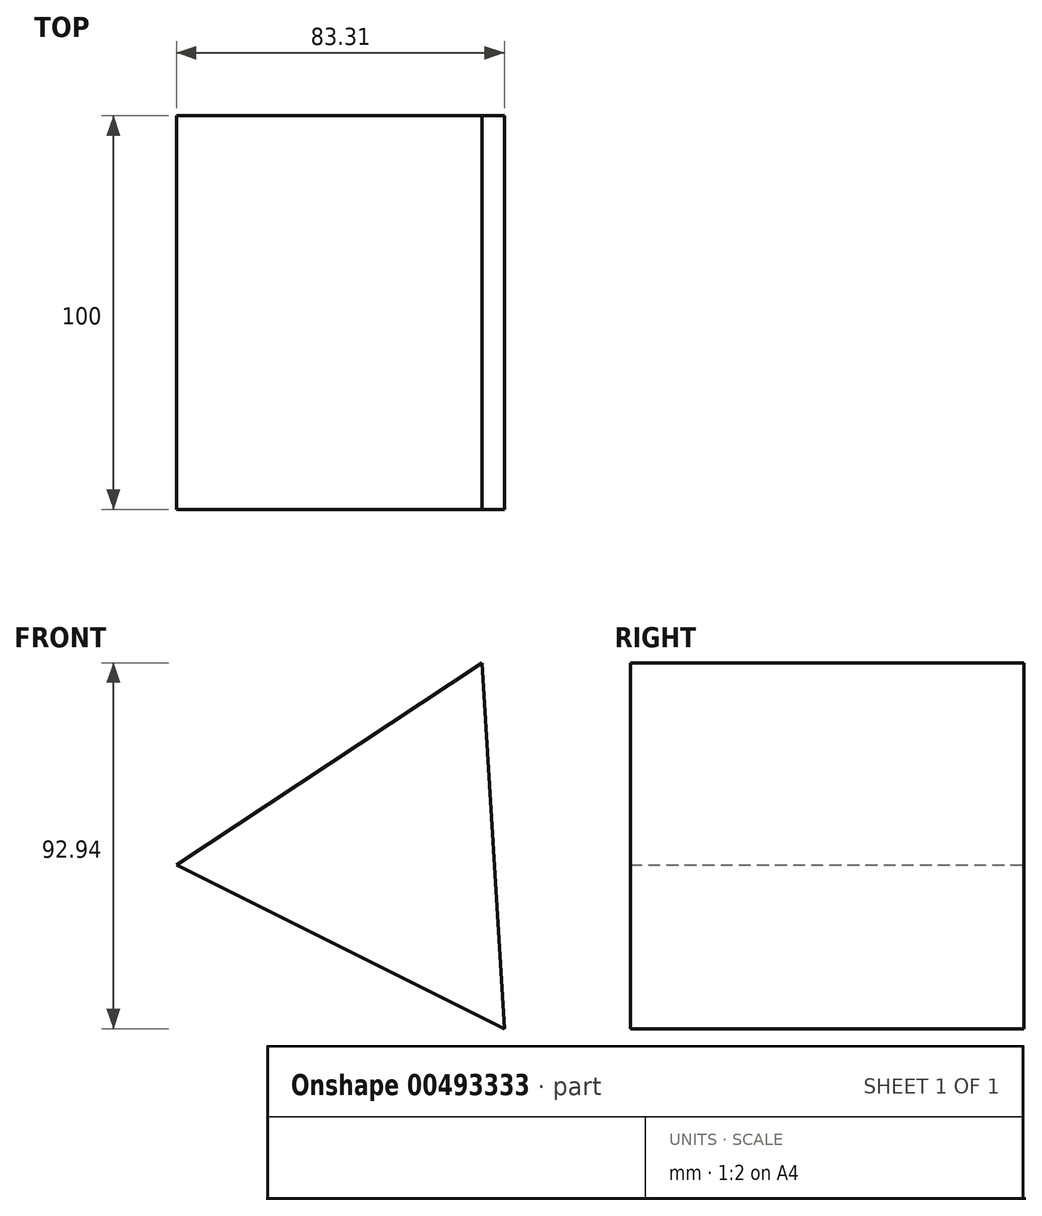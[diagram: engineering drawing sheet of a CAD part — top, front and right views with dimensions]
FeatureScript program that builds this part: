
annotation { "Feature Type Name" : "Feature", "Feature Type Description" : "" }
export const myFeature = defineFeature(function(context is Context, id is Id, definition is map)
    precondition{}
    {
        {
            var Q0;
            Q0=qCreatedBy(makeId("Front.planeOp"),FACE);
            var sketch = newSketch(context, id + "F0", { "sketchPlane" : qUnion([Q0])});
            skCircle(sketch, "E0.cCircle", {"center": v(0, 3.25) * mm, "radius": 53.76 * mm, "construction": true});
            skLineSegment(sketch, "E0.0", {"start": v(-53.66, 0) * mm, "end": v(24.01, 51.35) * mm});
            skLineSegment(sketch, "E0.1", {"start": v(24.01, 51.35) * mm, "end": v(29.65, -41.6) * mm});
            skLineSegment(sketch, "E0.2", {"start": v(29.65, -41.6) * mm, "end": v(-53.66, 0) * mm});
            skSolve(sketch);
        }
        {
            var Q0;
            Q0=makeQuery(id+"F0.imprint","IMPRINT",FACE,{"disambiguationData":[TD([[makeQuery(id+"F0.imprint","IMPRINT",EDGE,{"derivedFrom":sQuery(id+"F0.wireOp",EDGE,"E0.0")}),-1.0]])]});
            extrude(context, id + "F1", {"entities" : qUnion([Q0]), "depth" : 100 * mm});
        }
    });
